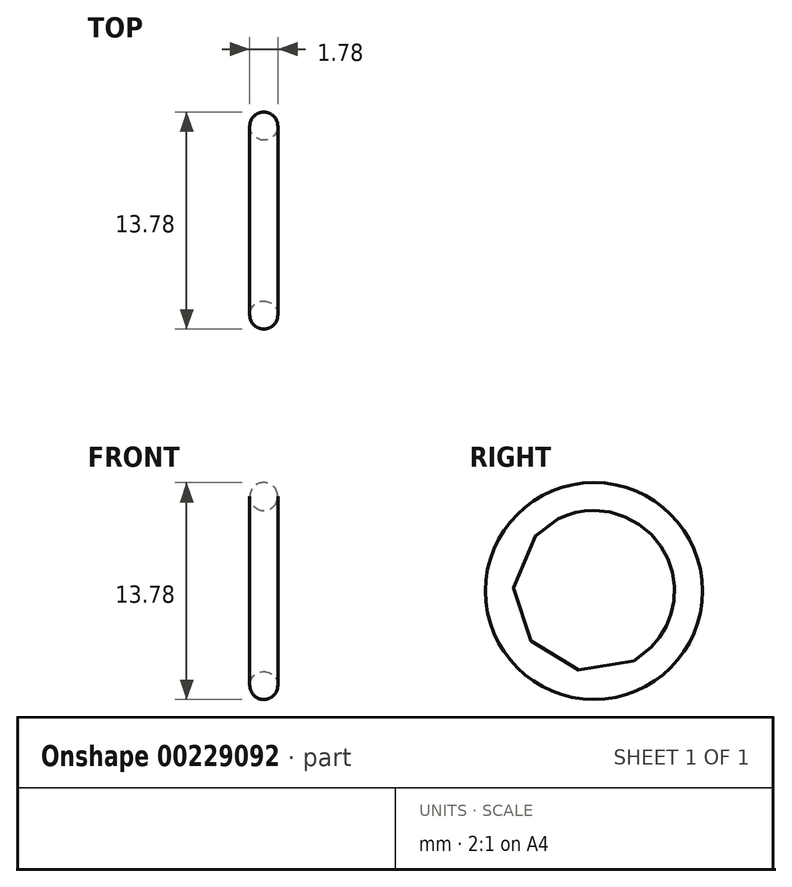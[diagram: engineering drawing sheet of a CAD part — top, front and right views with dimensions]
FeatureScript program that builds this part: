
annotation { "Feature Type Name" : "Feature", "Feature Type Description" : "" }
export const myFeature = defineFeature(function(context is Context, id is Id, definition is map)
    precondition{}
    {
        {
            var Q0;
            Q0=qCreatedBy(makeId("Front.planeOp"),FACE);
            var sketch = newSketch(context, id + "F0", { "sketchPlane" : qUnion([Q0])});
            skCircle(sketch, "E0", {"center": v(0, 6) * mm, "radius": 0.89 * mm});
            skLineSegment(sketch, "E1", {"start": v(-2.75, 0) * mm, "end": v(2.84, 0) * mm});
            skSolve(sketch);
        }
        {
            var Q0;
            Q0=makeQuery(id+"F0.imprint","IMPRINT",FACE,{"disambiguationData":[TD([[makeQuery(id+"F0.imprint","IMPRINT",EDGE,{"derivedFrom":sQuery(id+"F0.wireOp",EDGE,"E0")}),1.0]])]});
            var Q1;
            Q1=sQuery(id+"F0.wireOp",EDGE,"E1");
            revolve(context, id + "F1", {"entities" : qUnion([Q0]), "axis" : qUnion([Q1]), "revolveType" : RevolveType.FULL});
        }
    });
